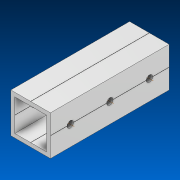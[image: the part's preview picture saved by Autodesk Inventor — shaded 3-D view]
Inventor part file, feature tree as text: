
AUTODESK INVENTOR PART (.ipt)
format: ipt  version: 2022.2 (Build 262287000, 287)  size: 637,440 bytes
history: native  units: in
note: dims shown in document units (in); Inventor stores cm internally (conversion verified against a paired STEP export)
features: other x3, extrude x1, pattern_linear x1, sketch x1, pattern_circular x1
ambient origin geometry x8: Origin, YZ Plane, XZ Plane, XY Plane, X Axis, Y Axis, Z Axis, Center Point
bodies: Solid1 (feature_tree)
feature tree (7):
  extrude  "Extrusion1"  Depth=1.0in
  other  "Work Axis1"
  pattern_linear  "Rectangular Pattern1"  Spacing1=0.0in  [1 undecoded]
  sketch  "Sketch1"  dims[d0=1.0in d1=56.0in d2=0.0in d3=1.1811in d5=1.0in]
  other  "Work Axis2"
  other  "Work Axis3"
  pattern_circular  "CirPattern2"
note: 1 required parameter value undecoded (feature->parameter linkage not recoverable at this tier; creation-order binding heuristic only, values carry confidence <= 0.55)
